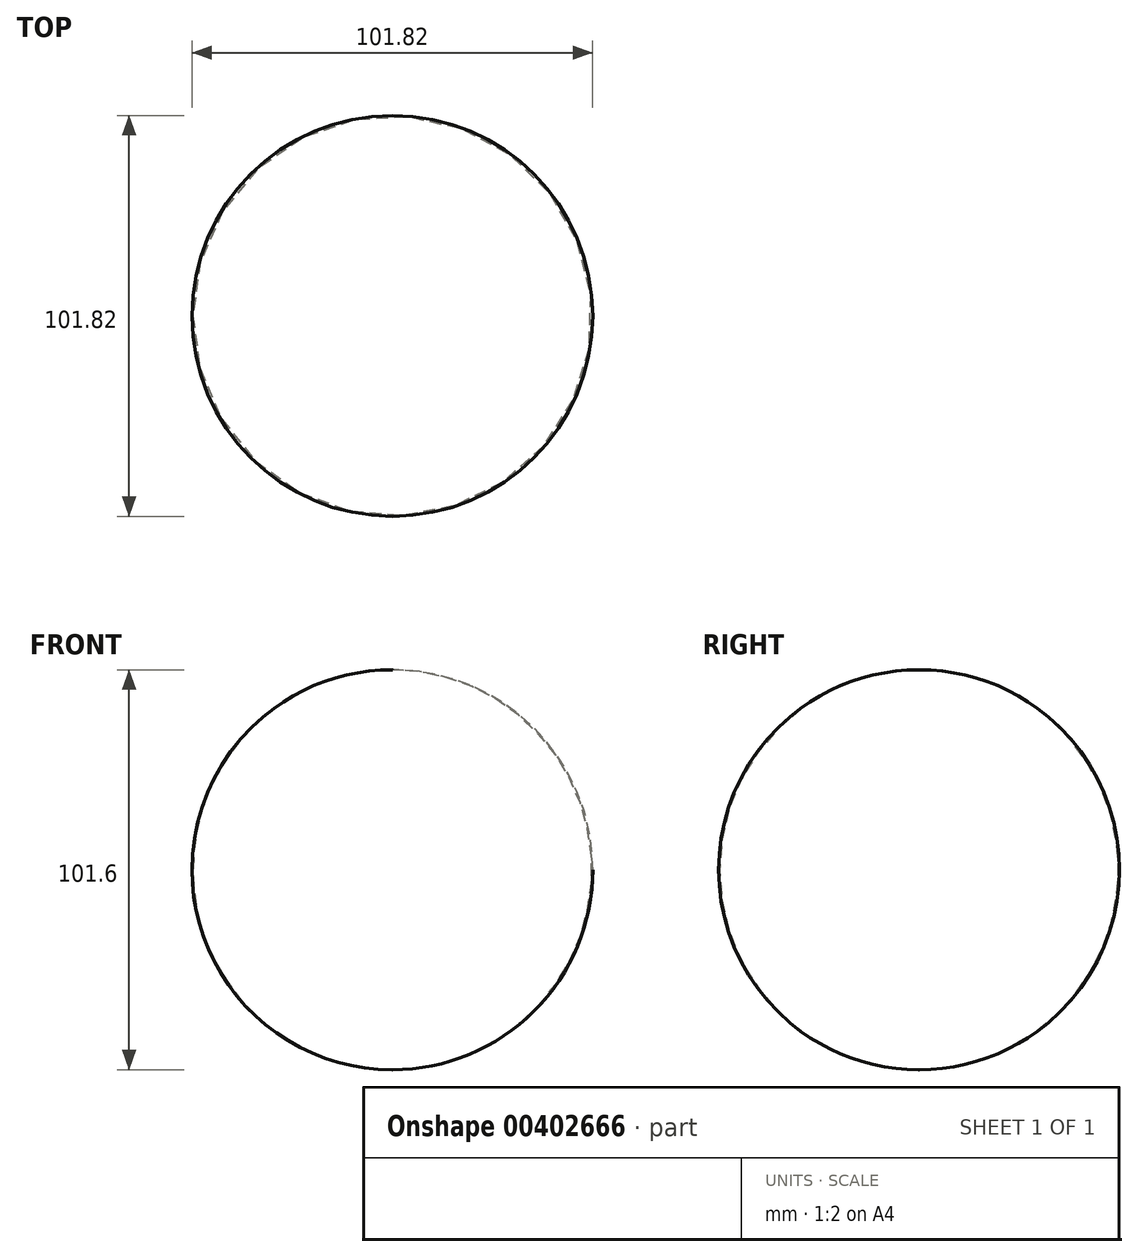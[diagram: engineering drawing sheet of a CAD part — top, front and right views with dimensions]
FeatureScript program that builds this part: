
annotation { "Feature Type Name" : "Feature", "Feature Type Description" : "" }
export const myFeature = defineFeature(function(context is Context, id is Id, definition is map)
    precondition{}
    {
        {
            var Q0;
            Q0=qCreatedBy(makeId("Front.planeOp"),FACE);
            var sketch = newSketch(context, id + "F0", { "sketchPlane" : qUnion([Q0])});
            skLineSegment(sketch, "E0", {"start": v(0, 50.8) * mm, "end": v(0, -50.8) * mm});
            skArc(sketch, "E1", {"start": v(0, -50.8) * mm, "mid": v(50.91, 0) * mm, "end": v(0, 50.8) * mm});
            skSolve(sketch);
        }
        {
            var Q0;
            Q0=makeQuery(id+"F0.imprint","IMPRINT",FACE,{"disambiguationData":[TD([[makeQuery(id+"F0.imprint","IMPRINT",EDGE,{"derivedFrom":sQuery(id+"F0.wireOp",EDGE,"E0")}),1.0]])]});
            var Q1;
            Q1=sQuery(id+"F0.wireOp",EDGE,"E0");
            revolve(context, id + "F1", {"entities" : qUnion([Q0]), "axis" : qUnion([Q1]), "revolveType" : RevolveType.FULL});
        }
    });
